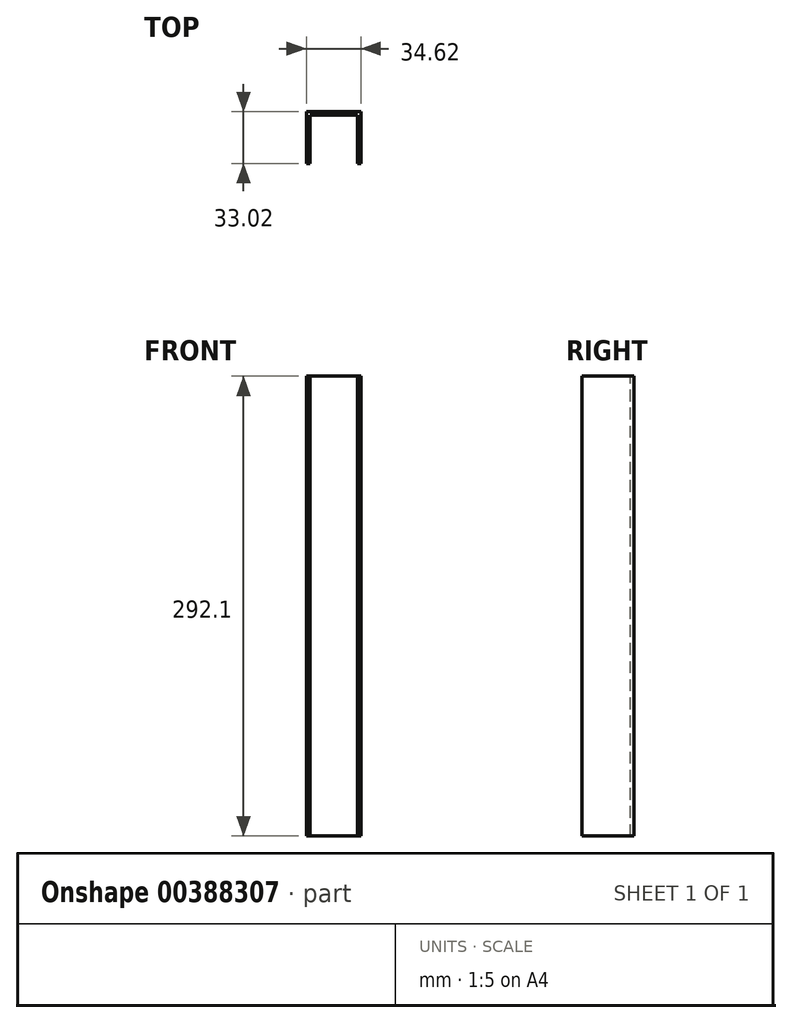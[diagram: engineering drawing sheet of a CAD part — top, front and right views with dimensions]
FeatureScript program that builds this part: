
annotation { "Feature Type Name" : "Feature", "Feature Type Description" : "" }
export const myFeature = defineFeature(function(context is Context, id is Id, definition is map)
    precondition{}
    {
        {
            var Q0;
            Q0=qCreatedBy(makeId("Front.planeOp"),FACE);
            var sketch = newSketch(context, id + "F0", { "sketchPlane" : qUnion([Q0])});
            skLineSegment(sketch, "E0", {"start": v(0, -76.4) * mm, "end": v(0, 215.7) * mm});
            skLineSegment(sketch, "E1", {"start": v(34.62, -76.4) * mm, "end": v(34.62, 215.7) * mm});
            skLineSegment(sketch, "E2", {"start": v(0, 215.7) * mm, "end": v(34.62, 215.7) * mm});
            skLineSegment(sketch, "E3", {"start": v(0, -76.4) * mm, "end": v(34.62, -76.4) * mm});
            skSolve(sketch);
        }
        {
            var Q0;
            Q0=qSketchRegion(id+"F0",true);
            extrude(context, id + "F1", {"entities" : qUnion([Q0]), "depth" : 33.02 * mm});
        }
        {
            var Q0;
            Q0=makeQuery(id+"F1.opExtrude","CAP_FACE",FACE,{"disambiguationData":[OSD([sQuery(id+"F0.wireOp",EDGE,"E0"),sQuery(id+"F0.wireOp",EDGE,"E1"),sQuery(id+"F0.wireOp",EDGE,"E2"),sQuery(id+"F0.wireOp",EDGE,"E3")])],"isStart":false});
            var Q1;
            Q1=makeQuery(id+"F1.opExtrude","SWEPT_FACE",FACE,{"disambiguationData":[OSD([sQuery(id+"F0.wireOp",EDGE,"E3")])]});
            var Q2;
            Q2=makeQuery(id+"F1.opExtrude","SWEPT_FACE",FACE,{"disambiguationData":[OSD([sQuery(id+"F0.wireOp",EDGE,"E2")])]});
            shell(context, id + "F2", {"entities" : qUnion([Q0, Q1, Q2]), "thickness" : 2.13 * mm});
        }
    });
